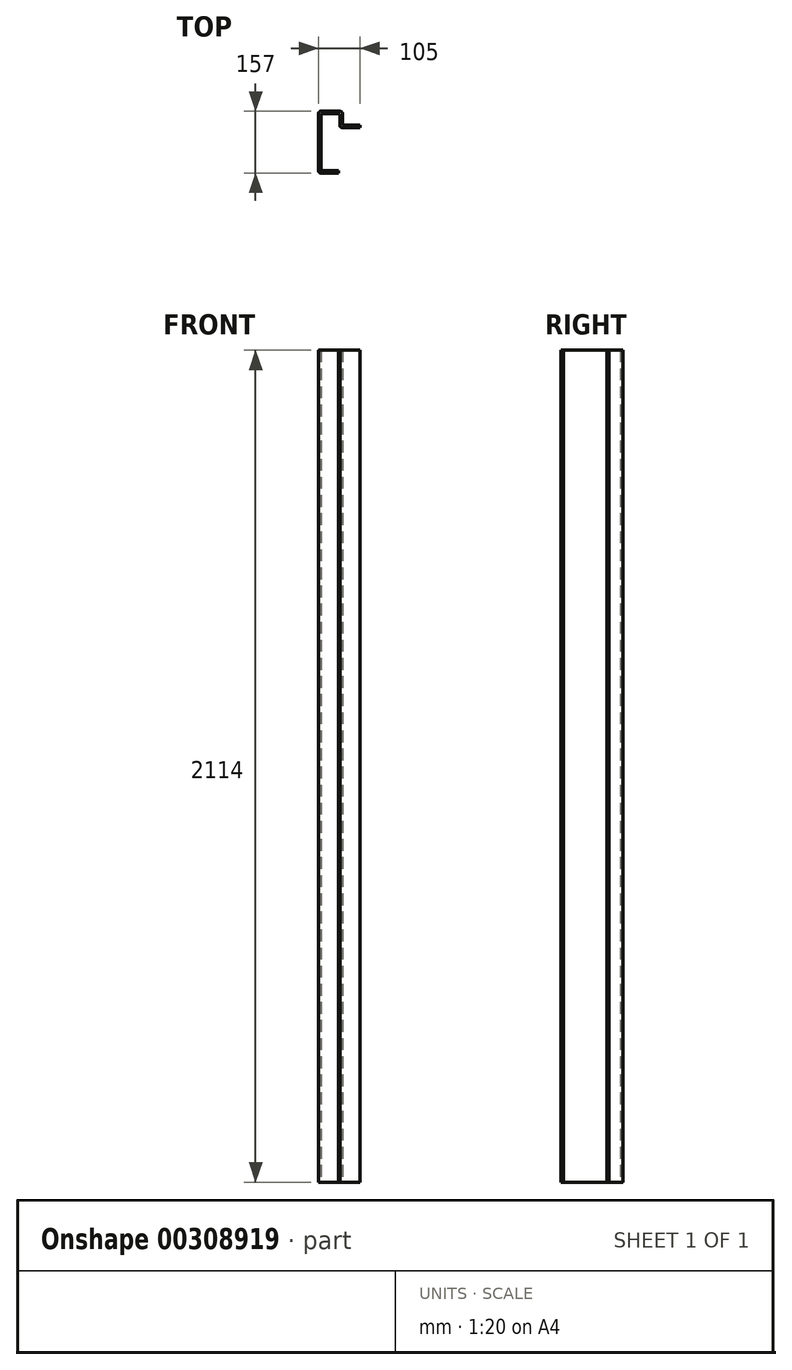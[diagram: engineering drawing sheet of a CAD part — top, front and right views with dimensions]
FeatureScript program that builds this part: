
annotation { "Feature Type Name" : "Feature", "Feature Type Description" : "" }
export const myFeature = defineFeature(function(context is Context, id is Id, definition is map)
    precondition{}
    {
        {
            var Q0;
            Q0=qCreatedBy(makeId("Top.planeOp"),FACE);
            var sketch = newSketch(context, id + "F0", { "sketchPlane" : qUnion([Q0])});
            skLineSegment(sketch, "E0", {"start": v(0, 0) * mm, "end": v(0, 6) * mm});
            skLineSegment(sketch, "E1", {"start": v(0, 0) * mm, "end": v(-45, 0) * mm});
            skLineSegment(sketch, "E2", {"start": v(-50, 5) * mm, "end": v(-50, 152) * mm});
            skLineSegment(sketch, "E3", {"start": v(-45, 157) * mm, "end": v(5, 157) * mm});
            skLineSegment(sketch, "E4", {"start": v(10, 152) * mm, "end": v(10, 127) * mm});
            skLineSegment(sketch, "E5", {"start": v(15, 122) * mm, "end": v(55, 122) * mm});
            skLineSegment(sketch, "E6", {"start": v(55, 122) * mm, "end": v(55, 116) * mm});
            skLineSegment(sketch, "E7.0", {"start": v(9, 116) * mm, "end": v(55, 116) * mm});
            skLineSegment(sketch, "E7.1", {"start": v(0, 6) * mm, "end": v(-39, 6) * mm});
            skLineSegment(sketch, "E7.2", {"start": v(-44, 11) * mm, "end": v(-44, 146) * mm});
            skLineSegment(sketch, "E7.3", {"start": v(-39, 151) * mm, "end": v(-1, 151) * mm});
            skLineSegment(sketch, "E7.4", {"start": v(4, 146) * mm, "end": v(4, 121) * mm});
            skPoint(sketch, "E8.visualSharp", {"position": v(4, 151) * mm});
            skArc(sketch, "E8.filletArc", {"start": v(4, 146) * mm, "mid": v(2.54, 149.54) * mm, "end": v(-1, 151) * mm});
            skPoint(sketch, "E9.visualSharp", {"position": v(10, 157) * mm});
            skArc(sketch, "E9.filletArc", {"start": v(10, 152) * mm, "mid": v(8.54, 155.54) * mm, "end": v(5, 157) * mm});
            skPoint(sketch, "E10.visualSharp", {"position": v(10, 122) * mm});
            skArc(sketch, "E10.filletArc", {"start": v(10, 127) * mm, "mid": v(11.46, 123.46) * mm, "end": v(15, 122) * mm});
            skPoint(sketch, "E11.visualSharp", {"position": v(4, 116) * mm});
            skArc(sketch, "E11.filletArc", {"start": v(4, 121) * mm, "mid": v(5.46, 117.46) * mm, "end": v(9, 116) * mm});
            skPoint(sketch, "E12.visualSharp", {"position": v(-44, 6) * mm});
            skArc(sketch, "E12.filletArc", {"start": v(-44, 11) * mm, "mid": v(-42.54, 7.46) * mm, "end": v(-39, 6) * mm});
            skPoint(sketch, "E13.visualSharp", {"position": v(-50, 0) * mm});
            skArc(sketch, "E13.filletArc", {"start": v(-50, 5) * mm, "mid": v(-48.54, 1.46) * mm, "end": v(-45, 0) * mm});
            skPoint(sketch, "E14.visualSharp", {"position": v(-50, 157) * mm});
            skArc(sketch, "E14.filletArc", {"start": v(-45, 157) * mm, "mid": v(-48.54, 155.54) * mm, "end": v(-50, 152) * mm});
            skPoint(sketch, "E15.visualSharp", {"position": v(-44, 151) * mm});
            skArc(sketch, "E15.filletArc", {"start": v(-39, 151) * mm, "mid": v(-42.54, 149.54) * mm, "end": v(-44, 146) * mm});
            skSolve(sketch);
        }
        {
            var Q0;
            Q0=makeQuery(id+"F0.imprint","IMPRINT",FACE,{"disambiguationData":[TD([[makeQuery(id+"F0.imprint","IMPRINT",EDGE,{"derivedFrom":sQuery(id+"F0.wireOp",EDGE,"E0")}),1.0]])]});
            extrude(context, id + "F1", {"entities" : qUnion([Q0]), "depth" : 2114 * mm});
        }
    });
